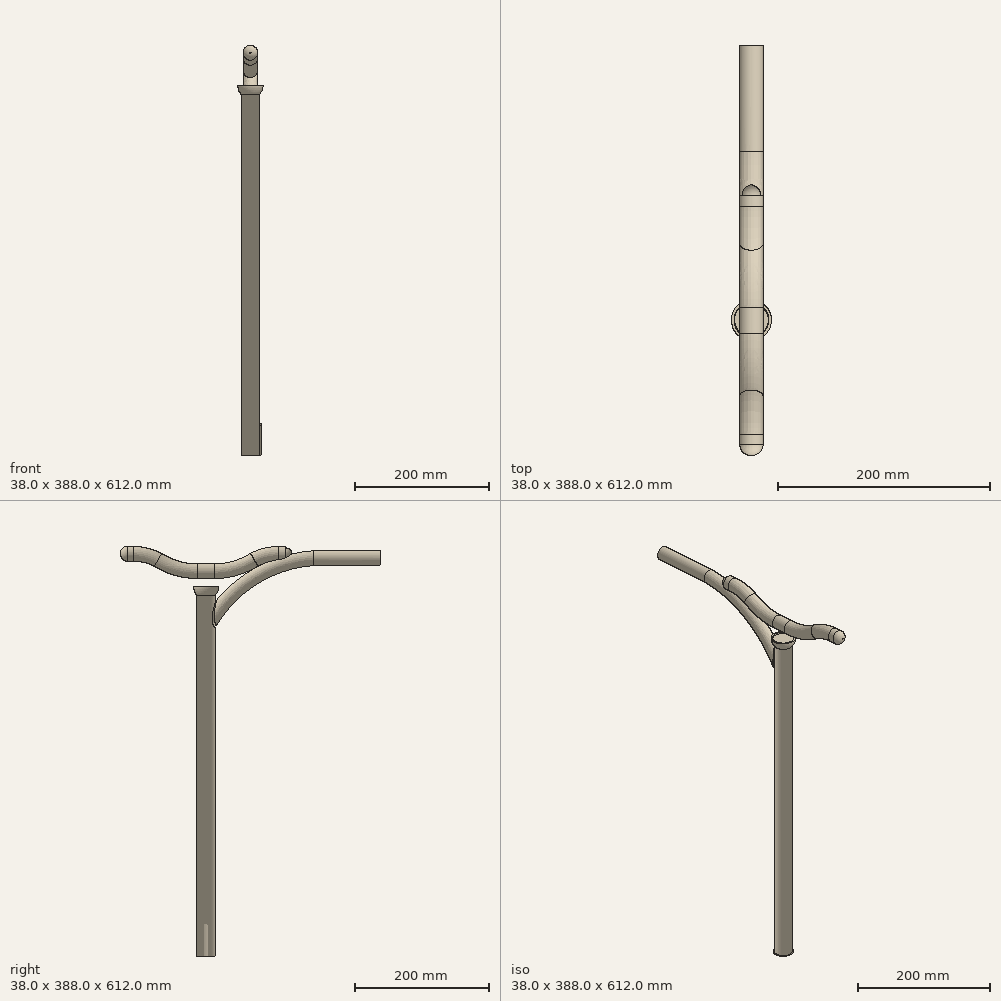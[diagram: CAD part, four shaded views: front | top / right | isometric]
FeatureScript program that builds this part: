
annotation { "Feature Type Name" : "Feature", "Feature Type Description" : "" }
export const myFeature = defineFeature(function(context is Context, id is Id, definition is map)
    precondition{}
    {
        {
            var Q0;
            Q0=qCreatedBy(makeId("Top.planeOp"),FACE);
            var sketch = newSketch(context, id + "F0", { "sketchPlane" : qUnion([Q0])});
            skCircle(sketch, "E0", {"center": v(0, 0) * mm, "radius": 16 * mm});
            skSolve(sketch);
        }
        {
            var Q0;
            Q0 = qSketchRegion(id + "F0", true);
            extrude(context, id + "F1", {"entities" : qUnion([Q0]), "depth" : 550 * mm, "offsetDistance" : 25 * mm});
        }
        {
            var Q0;
            Q0=makeQuery(id+"F1.opExtrude","CAP_FACE",FACE,{"disambiguationData":[OSD([sQuery(id+"F0.wireOp",EDGE,"E0")])],"isStart":true});
            shell(context, id + "F2", {"entities" : qUnion([Q0]), "thickness" : 2 * mm});
        }
        {
            var Q0;
            Q0=qCreatedBy(makeId("Right.planeOp"),FACE);
            var sketch = newSketch(context, id + "F3", { "sketchPlane" : qUnion([Q0])});
            skLineSegment(sketch, "E1.bottom", {"start": v(-2.95, 0) * mm, "end": v(3.05, 0) * mm});
            skLineSegment(sketch, "E1.left", {"start": v(-2.95, 0) * mm, "end": v(-2.95, 45) * mm});
            skLineSegment(sketch, "E1.right", {"start": v(3.05, 0) * mm, "end": v(3.05, 45) * mm});
            skArc(sketch, "E2", {"start": v(3.05, 45) * mm, "mid": v(0.05, 48) * mm, "end": v(-2.95, 45) * mm});
            skSolve(sketch);
        }
        {
            var Q0;
            Q0 = qSketchRegion(id + "F3", true);
            extrude(context, id + "F4", {"entities" : qUnion([Q0]), "operationType" : NewBodyOperationType.REMOVE, "endBound" : BoundingType.THROUGH_ALL, "depth" : 25 * mm, "offsetDistance" : 25 * mm});
        }
        {
            var Q0;
            Q0=qCreatedBy(makeId("Right.planeOp"),FACE);
            var sketch = newSketch(context, id + "F5", { "sketchPlane" : qUnion([Q0])});
            skArc(sketch, "E3", {"start": v(160, 594.48) * mm, "mid": v(65.9, 562.14) * mm, "end": v(0, 487.58) * mm});
            skLineSegment(sketch, "E4", {"start": v(160, 594.48) * mm, "end": v(260, 594.48) * mm});
            skSolve(sketch);
        }
        {
            var Q0;
            Q0=sQuery(id+"F5.wireOp",VERTEX,"E4.end");
            var Q1;
            Q1=qCreatedBy(makeId("Front.planeOp"),FACE);
            cPlane(context, id + "F6", {"entities" : qUnion([Q0, Q1]), "cplaneType" : CPlaneType.PLANE_POINT, "offset" : 25 * mm, "width" : 150 * mm, "height" : 150 * mm});
        }
        {
            var Q0;
            Q0=qCreatedBy(id+"F6.planeOp",FACE);
            var sketch = newSketch(context, id + "F7", { "sketchPlane" : qUnion([Q0])});
            skCircle(sketch, "E5", {"center": v(0, 594.51) * mm, "radius": 11 * mm});
            skLineSegment(sketch, "E6", {"start": v(0, 594.51) * mm, "end": v(0, 594.51) * mm});
            skSolve(sketch);
        }
        {
            var Q0;
            Q0 = qSketchRegion(id + "F7", true);
            var Q1;
            Q1 = qConstructionFilter(qBodyType(qCreatedBy(id + "F5" ,EDGE), BodyType.WIRE), ConstructionObject.NO);
            sweep(context, id + "F8", {"operationType" : NewBodyOperationType.ADD, "profiles" : qUnion([Q0]), "path" : qUnion([Q1])});
        }
        {
            var Q0;
            Q0=makeQuery(id+"F8.opSweep","CAP_FACE",FACE,{"disambiguationData":[OSD([sQuery(id+"F5.wireOp",VERTEX,"E4.end"),sQuery(id+"F7.wireOp",EDGE,"E5")])],"isStart":true});
            shell(context, id + "F9", {"entities" : qUnion([Q0]), "thickness" : 2 * mm});
        }
        {
            var Q0;
            Q0=qCreatedBy(makeId("Right.planeOp"),FACE);
            var sketch = newSketch(context, id + "F10", { "sketchPlane" : qUnion([Q0])});
            skLineSegment(sketch, "E7", {"start": v(0, 575) * mm, "end": v(-12.5, 575) * mm});
            skArc(sketch, "E8", {"start": v(-71.73, 591.94) * mm, "mid": v(-43.3, 579.32) * mm, "end": v(-12.5, 575) * mm});
            skLineSegment(sketch, "E9", {"start": v(-108, 601) * mm, "end": v(-128, 601) * mm});
            skArc(sketch, "E10", {"start": v(-71.73, 591.94) * mm, "mid": v(-89.3, 598.7) * mm, "end": v(-108, 601) * mm});
            skLineSegment(sketch, "E11.MirrorCS", {"start": v(0, 575) * mm, "end": v(12.5, 575) * mm});
            skArc(sketch, "E12.MirrorCS", {"start": v(71.73, 591.94) * mm, "mid": v(43.3, 579.32) * mm, "end": v(12.5, 575) * mm});
            skArc(sketch, "E13.MirrorCS", {"start": v(71.73, 591.94) * mm, "mid": v(89.3, 598.7) * mm, "end": v(108, 601) * mm});
            skLineSegment(sketch, "E14.MirrorCS", {"start": v(108, 601) * mm, "end": v(128, 601) * mm});
            skSolve(sketch);
        }
        {
            var Q0;
            Q0=sQuery(id+"F10.wireOp",VERTEX,"E14.MirrorCS.end");
            var Q1;
            Q1=qCreatedBy(id+"F6.planeOp",FACE);
            cPlane(context, id + "F11", {"entities" : qUnion([Q0, Q1]), "cplaneType" : CPlaneType.PLANE_POINT, "offset" : 25 * mm, "width" : 150 * mm, "height" : 150 * mm});
        }
        {
            var Q0;
            Q0=qCreatedBy(id+"F11.planeOp",FACE);
            var sketch = newSketch(context, id + "F12", { "sketchPlane" : qUnion([Q0])});
            skCircle(sketch, "E15", {"center": v(0, 601) * mm, "radius": 11 * mm});
            skSolve(sketch);
        }
        {
            var Q0;
            Q0=makeQuery(id+"F12.imprint","IMPRINT",FACE,{"disambiguationData":[TD([[makeQuery(id+"F12.imprint","IMPRINT",EDGE,{"derivedFrom":sQuery(id+"F12.wireOp",EDGE,"E15")}),1.0]])]});
            var Q1;
            Q1 = qConstructionFilter(qBodyType(qCreatedBy(id + "F10" ,EDGE), BodyType.WIRE), ConstructionObject.NO);
            sweep(context, id + "F13", {"profiles" : qUnion([Q0]), "path" : qUnion([Q1])});
        }
        {
            var Q0;
            Q0=makeQuery(id+"F13.opSweep","CAP_EDGE",EDGE,{"disambiguationData":[OSD([sQuery(id+"F10.wireOp",VERTEX,"E9.end"),sQuery(id+"F12.wireOp",EDGE,"E15")])],"isStart":false});
            var Q1;
            Q1=makeQuery(id+"F13.opSweep","CAP_EDGE",EDGE,{"disambiguationData":[OSD([sQuery(id+"F10.wireOp",VERTEX,"E14.MirrorCS.end"),sQuery(id+"F12.wireOp",EDGE,"E15")])],"isStart":true});
            fillet(context, id + "F14", {"entities" : qUnion([Q0, Q1]), "radius" : 10 * mm, "tangentPropagation" : true, "allowEdgeOverflow" : false});
        }
        {
            var Q0;
            Q0=qCreatedBy(makeId("Right.planeOp"),FACE);
            var sketch = newSketch(context, id + "F15", { "sketchPlane" : qUnion([Q0])});
            skArc(sketch, "E16", {"start": v(-19, 552) * mm, "mid": v(-13.44, 538.56) * mm, "end": v(0, 533) * mm});
            skLineSegment(sketch, "E17", {"start": v(0, 552) * mm, "end": v(-19, 552) * mm});
            skLineSegment(sketch, "E18", {"start": v(0, 552) * mm, "end": v(0, 533) * mm});
            skSolve(sketch);
        }
        {
            var Q0;
            Q0 = qSketchRegion(id + "F15", true);
            var Q1;
            Q1=makeQuery(id+"F1.opExtrude","CAP_EDGE",EDGE,{"disambiguationData":[OSD([sQuery(id+"F0.wireOp",EDGE,"E0")])],"isStart":false});
            revolve(context, id + "F16", {"surfaceOperationType" : NewSurfaceOperationType.NEW, "entities" : qUnion([Q0]), "axis" : qUnion([Q1]), "revolveType" : RevolveType.FULL});
        }
        {
            var Q0;
            Q0=makeQuery(id+"F16.opRevolve","SWEPT_FACE",FACE,{"disambiguationData":[OSD([sQuery(id+"F15.wireOp",EDGE,"E17")])]});
            shell(context, id + "F17", {"entities" : qUnion([Q0]), "thickness" : 2.5 * mm});
        }
    });
